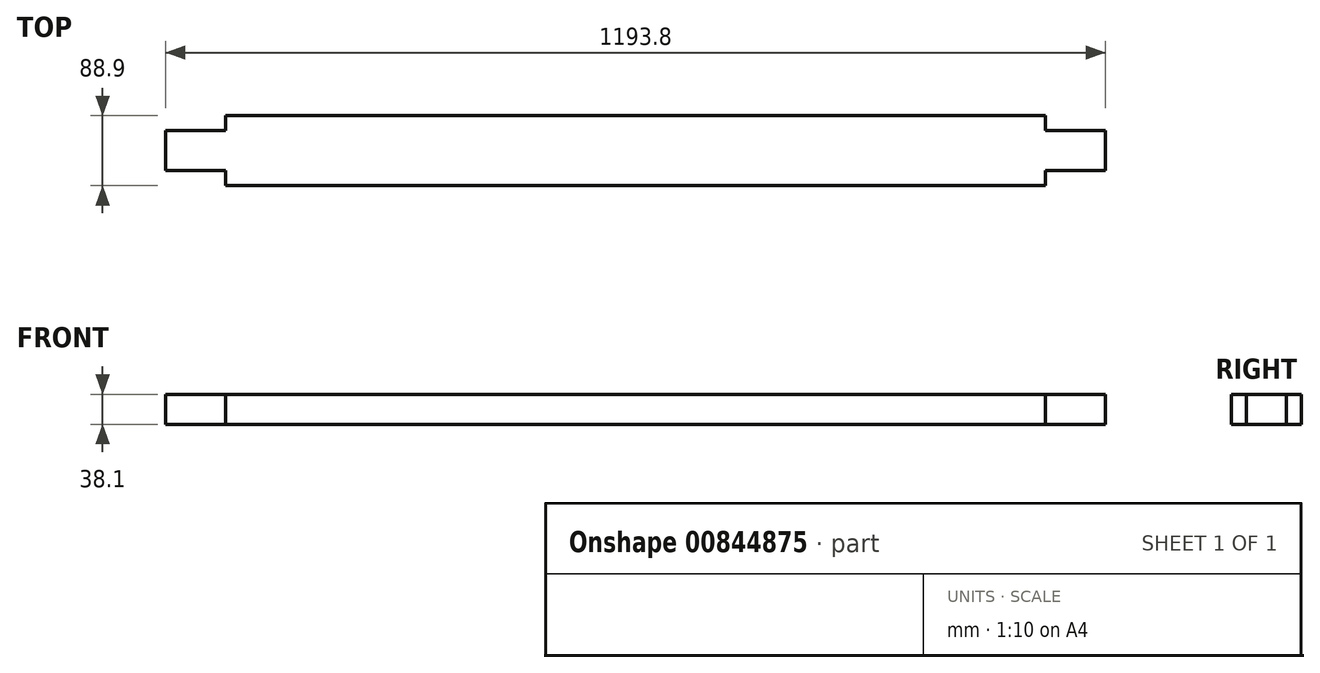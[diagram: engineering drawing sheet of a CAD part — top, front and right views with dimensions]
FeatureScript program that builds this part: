
annotation { "Feature Type Name" : "Feature", "Feature Type Description" : "" }
export const myFeature = defineFeature(function(context is Context, id is Id, definition is map)
    precondition{}
    {
        {
            var Q0;
            Q0=qCreatedBy(makeId("Right.planeOp"),FACE);
            var sketch = newSketch(context, id + "F0", { "sketchPlane" : qUnion([Q0])});
            skLineSegment(sketch, "E0.bottom", {"start": v(0, 0) * mm, "end": v(88.9, 0) * mm});
            skLineSegment(sketch, "E0.top", {"start": v(0, 38.1) * mm, "end": v(88.9, 38.1) * mm});
            skLineSegment(sketch, "E0.left", {"start": v(0, 0) * mm, "end": v(0, 38.1) * mm});
            skLineSegment(sketch, "E0.right", {"start": v(88.9, 0) * mm, "end": v(88.9, 38.1) * mm});
            skSolve(sketch);
        }
        {
            var Q0;
            Q0 = qSketchRegion(id + "F0", true);
            extrude(context, id + "F1", {"entities" : qUnion([Q0]), "oppositeDirection" : true, "depth" : 1041.4 * mm, "offsetDistance" : 25.4 * mm});
        }
        {
            var Q0;
            Q0=makeQuery(id+"F1.opExtrude","CAP_FACE",FACE,{"disambiguationData":[OSD([sQuery(id+"F0.wireOp",EDGE,"E0.bottom"),sQuery(id+"F0.wireOp",EDGE,"E0.top"),sQuery(id+"F0.wireOp",EDGE,"E0.left"),sQuery(id+"F0.wireOp",EDGE,"E0.right")])],"isStart":true});
            var sketch = newSketch(context, id + "F2", { "sketchPlane" : qUnion([Q0])});
            skLineSegment(sketch, "E1.bottom", {"start": v(19.05, 38.1) * mm, "end": v(69.85, 38.1) * mm});
            skLineSegment(sketch, "E1.top", {"start": v(19.05, 0) * mm, "end": v(69.85, 0) * mm});
            skLineSegment(sketch, "E1.left", {"start": v(19.05, 38.1) * mm, "end": v(19.05, 0) * mm});
            skLineSegment(sketch, "E1.right", {"start": v(69.85, 38.1) * mm, "end": v(69.85, 0) * mm});
            skSolve(sketch);
        }
        {
            var Q0;
            Q0=makeQuery(id+"F2.imprint","IMPRINT",FACE,{"disambiguationData":[TD([[makeQuery(id+"F2.imprint","IMPRINT",EDGE,{"derivedFrom":sQuery(id+"F2.wireOp",EDGE,"E1.bottom")}),-1.0]])]});
            extrude(context, id + "F3", {"entities" : qUnion([Q0]), "operationType" : NewBodyOperationType.ADD, "depth" : 76.2 * mm, "offsetDistance" : 25.4 * mm});
        }
        {
            var Q0;
            Q0=makeQuery(id+"F1.opExtrude","CAP_FACE",FACE,{"disambiguationData":[OSD([sQuery(id+"F0.wireOp",EDGE,"E0.bottom"),sQuery(id+"F0.wireOp",EDGE,"E0.top"),sQuery(id+"F0.wireOp",EDGE,"E0.left"),sQuery(id+"F0.wireOp",EDGE,"E0.right")])],"isStart":false});
            var sketch = newSketch(context, id + "F4", { "sketchPlane" : qUnion([Q0])});
            skLineSegment(sketch, "E2.bottom", {"start": v(-69.85, 38.1) * mm, "end": v(-19.05, 38.1) * mm});
            skLineSegment(sketch, "E2.top", {"start": v(-69.85, 0) * mm, "end": v(-19.05, 0) * mm});
            skLineSegment(sketch, "E2.left", {"start": v(-69.85, 38.1) * mm, "end": v(-69.85, 0) * mm});
            skLineSegment(sketch, "E2.right", {"start": v(-19.05, 38.1) * mm, "end": v(-19.05, 0) * mm});
            skSolve(sketch);
        }
        {
            var Q0;
            Q0=makeQuery(id+"F4.imprint","IMPRINT",FACE,{"disambiguationData":[TD([[makeQuery(id+"F4.imprint","IMPRINT",EDGE,{"derivedFrom":sQuery(id+"F4.wireOp",EDGE,"E2.bottom")}),1.0]])]});
            extrude(context, id + "F5", {"entities" : qUnion([Q0]), "operationType" : NewBodyOperationType.ADD, "depth" : 76.2 * mm, "offsetDistance" : 25.4 * mm});
        }
    });
